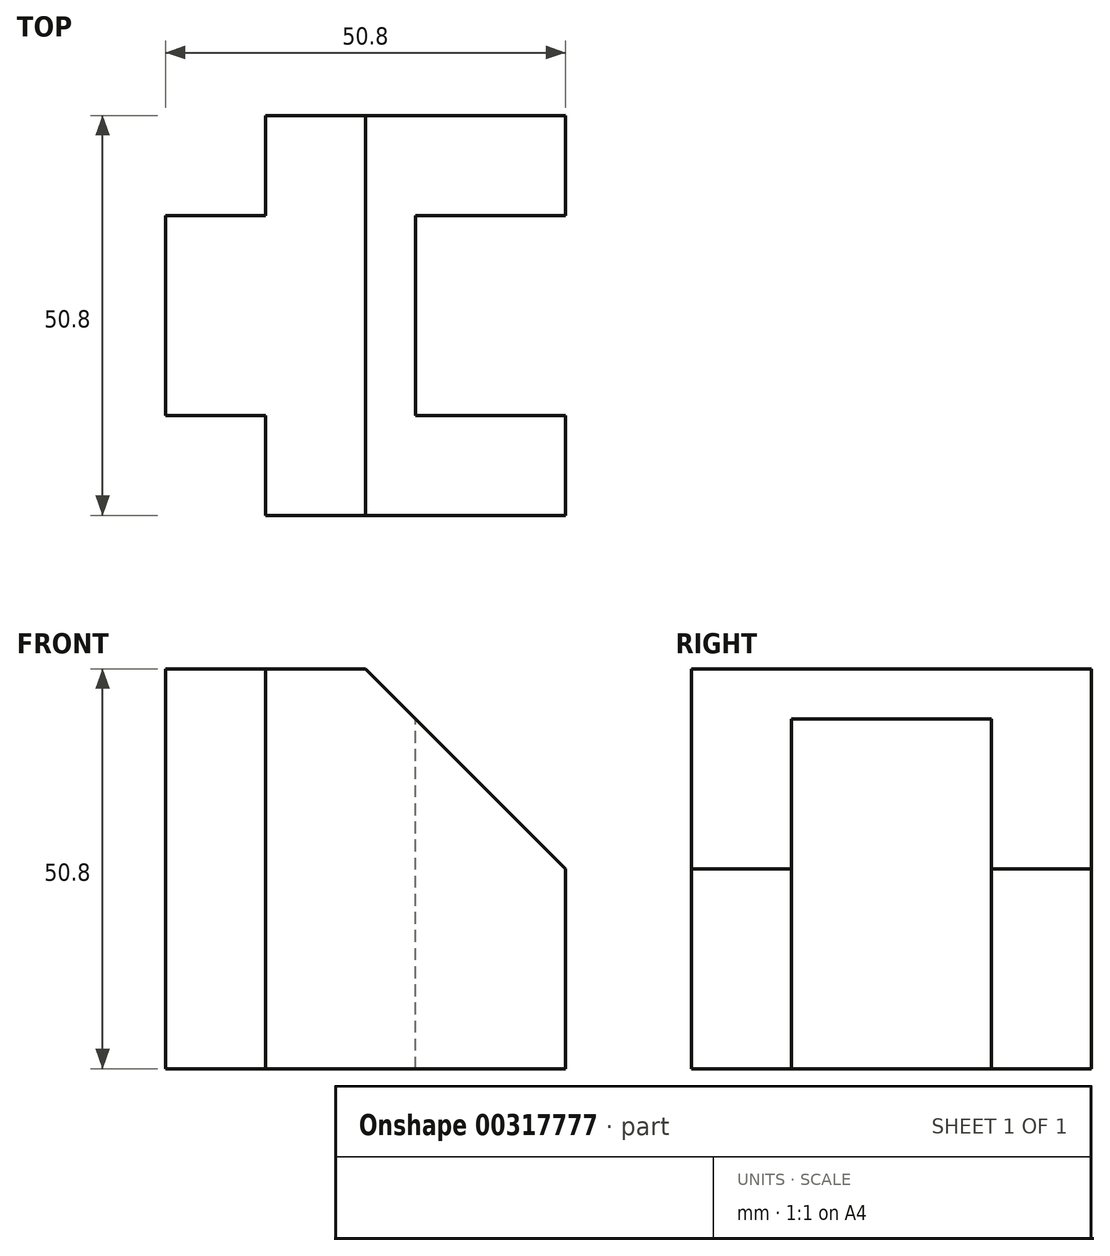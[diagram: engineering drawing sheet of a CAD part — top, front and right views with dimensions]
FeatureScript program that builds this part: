
annotation { "Feature Type Name" : "Feature", "Feature Type Description" : "" }
export const myFeature = defineFeature(function(context is Context, id is Id, definition is map)
    precondition{}
    {
        {
            var Q0;
            Q0=qCreatedBy(makeId("Top.planeOp"),FACE);
            var sketch = newSketch(context, id + "F0", { "sketchPlane" : qUnion([Q0])});
            skLineSegment(sketch, "E0", {"start": v(0, 0) * mm, "end": v(0, 12.7) * mm});
            skLineSegment(sketch, "E1", {"start": v(0, 12.7) * mm, "end": v(12.7, 12.7) * mm});
            skLineSegment(sketch, "E2", {"start": v(12.7, 12.7) * mm, "end": v(12.7, 25.4) * mm});
            skLineSegment(sketch, "E3", {"start": v(12.7, 25.4) * mm, "end": v(50.8, 25.4) * mm});
            skLineSegment(sketch, "E4", {"start": v(50.8, 25.4) * mm, "end": v(50.8, 0) * mm});
            skLineSegment(sketch, "E5", {"start": v(0, 0) * mm, "end": v(67.96, 0) * mm, "construction": true});
            skLineSegment(sketch, "E6.MirrorCS", {"start": v(0, 0) * mm, "end": v(0, -12.7) * mm});
            skLineSegment(sketch, "E7.MirrorCS", {"start": v(0, -12.7) * mm, "end": v(12.7, -12.7) * mm});
            skLineSegment(sketch, "E8.MirrorCS", {"start": v(12.7, -12.7) * mm, "end": v(12.7, -25.4) * mm});
            skLineSegment(sketch, "E9.MirrorCS", {"start": v(12.7, -25.4) * mm, "end": v(50.8, -25.4) * mm});
            skLineSegment(sketch, "E10.MirrorCS", {"start": v(50.8, -25.4) * mm, "end": v(50.8, 0) * mm});
            skSolve(sketch);
        }
        {
            var Q0;
            Q0=makeQuery(id+"F0.imprint","IMPRINT",FACE,{"disambiguationData":[TD([[makeQuery(id+"F0.imprint","IMPRINT",EDGE,{"derivedFrom":sQuery(id+"F0.wireOp",EDGE,"E0")}),-1.0]])]});
            extrude(context, id + "F1", {"entities" : qUnion([Q0]), "depth" : 50.8 * mm});
        }
        {
            var Q0;
            Q0=makeQuery(id+"F1.opExtrude","CAP_FACE",FACE,{"disambiguationData":[OSD([sQuery(id+"F0.wireOp",EDGE,"E0"),sQuery(id+"F0.wireOp",EDGE,"E1"),sQuery(id+"F0.wireOp",EDGE,"E2"),sQuery(id+"F0.wireOp",EDGE,"E3"),sQuery(id+"F0.wireOp",EDGE,"E4"),sQuery(id+"F0.wireOp",EDGE,"E6.MirrorCS"),sQuery(id+"F0.wireOp",EDGE,"E7.MirrorCS"),sQuery(id+"F0.wireOp",EDGE,"E8.MirrorCS"),sQuery(id+"F0.wireOp",EDGE,"E9.MirrorCS"),sQuery(id+"F0.wireOp",EDGE,"E10.MirrorCS")])],"isStart":false});
            var sketch = newSketch(context, id + "F2", { "sketchPlane" : qUnion([Q0])});
            skLineSegment(sketch, "E11", {"start": v(0, 0) * mm, "end": v(65.8, 0) * mm, "construction": true});
            skLineSegment(sketch, "E12", {"start": v(50.8, 12.7) * mm, "end": v(31.75, 12.7) * mm});
            skLineSegment(sketch, "E13", {"start": v(31.75, 12.7) * mm, "end": v(31.75, 0) * mm});
            skLineSegment(sketch, "E14", {"start": v(50.8, 12.7) * mm, "end": v(50.8, 0) * mm});
            skLineSegment(sketch, "E15.MirrorCS", {"start": v(31.75, -12.7) * mm, "end": v(31.75, 0) * mm});
            skLineSegment(sketch, "E16.MirrorCS", {"start": v(50.8, -12.7) * mm, "end": v(31.75, -12.7) * mm});
            skLineSegment(sketch, "E17.MirrorCS", {"start": v(50.8, -12.7) * mm, "end": v(50.8, 0) * mm});
            skSolve(sketch);
        }
        {
            var Q0;
            Q0=makeQuery(id+"F2.imprint","IMPRINT",FACE,{"disambiguationData":[TD([[makeQuery(id+"F2.imprint","IMPRINT",EDGE,{"derivedFrom":sQuery(id+"F2.wireOp",EDGE,"E12")}),1.0]])]});
            extrude(context, id + "F3", {"entities" : qUnion([Q0]), "operationType" : NewBodyOperationType.REMOVE, "oppositeDirection" : true, "depth" : 63.5 * mm});
        }
        {
            var Q0;
            Q0=makeQuery(id+"F1.opExtrude","SWEPT_FACE",FACE,{"disambiguationData":[OSD([sQuery(id+"F0.wireOp",EDGE,"E9.MirrorCS")])]});
            var sketch = newSketch(context, id + "F4", { "sketchPlane" : qUnion([Q0])});
            skLineSegment(sketch, "E18", {"start": v(50.8, 50.8) * mm, "end": v(25.4, 50.8) * mm});
            skLineSegment(sketch, "E19", {"start": v(25.4, 50.8) * mm, "end": v(50.8, 25.4) * mm});
            skLineSegment(sketch, "E20", {"start": v(50.8, 25.4) * mm, "end": v(50.8, 50.8) * mm});
            skSolve(sketch);
        }
        {
            var Q0;
            Q0=makeQuery(id+"F4.imprint","IMPRINT",FACE,{"disambiguationData":[TD([[makeQuery(id+"F4.imprint","IMPRINT",EDGE,{"derivedFrom":sQuery(id+"F4.wireOp",EDGE,"E18")}),-1.0]])]});
            extrude(context, id + "F5", {"entities" : qUnion([Q0]), "operationType" : NewBodyOperationType.REMOVE, "endBound" : BoundingType.THROUGH_ALL, "oppositeDirection" : true, "depth" : 25.4 * mm});
        }
    });
